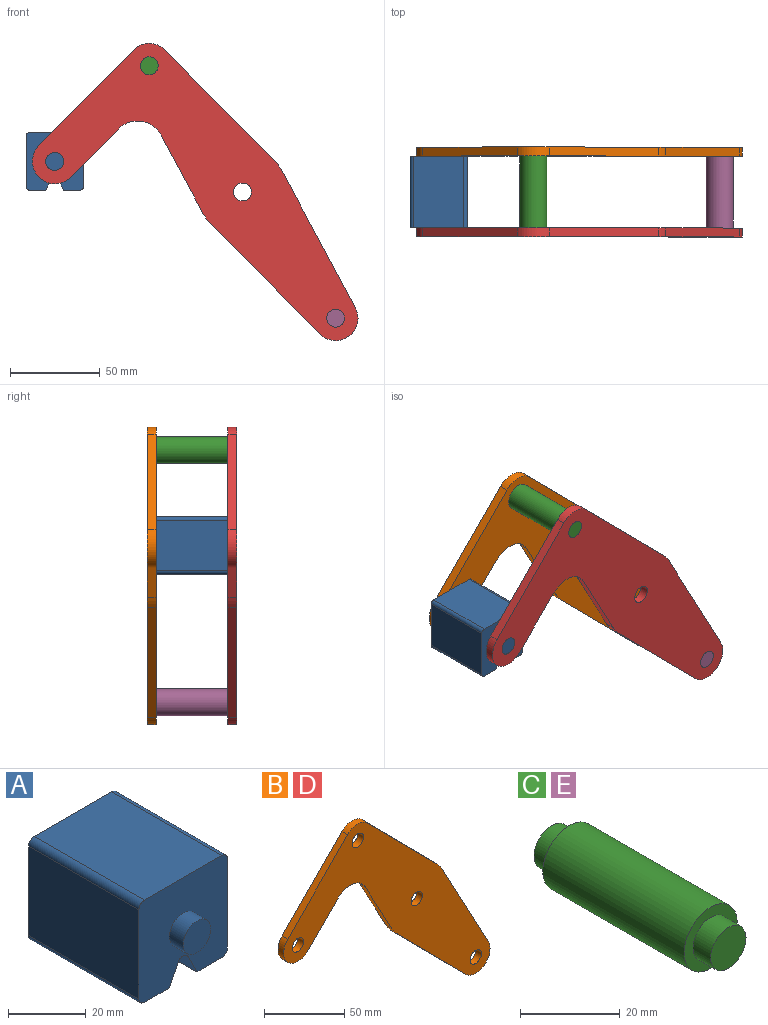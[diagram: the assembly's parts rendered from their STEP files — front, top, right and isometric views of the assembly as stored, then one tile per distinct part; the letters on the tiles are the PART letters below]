
ASSEMBLY  parts=5 mates=3
PART A: 18 faces, bbox 32.1x50x32.1 mm
  f0: plane 40x28.08mm, normal (1,0,0), area 1123.1mm2, adj f4,f10,f13,f14
  f1: plane 40x9.04mm, normal (0,0,-1), area 361.6mm2, adj f2,f4,f10,f14
  f2: plane 40x6.42mm, normal (-0.89,0,-0.45), area 287.2mm2, adj f1,f4,f10,f15
  f3: plane 40x6.42mm, normal (0.89,0,-0.45), area 287.2mm2, adj f4,f5,f10,f15
  f4: plane 32.08x32.08mm, normal (0,-1,0), area 900.6mm2, adj f0,f1,f2,f3,f5,f6,f7,f9
  f5: plane 40x9.04mm, normal (0,0,-1), area 361.6mm2, adj f3,f4,f10,f16
  f6: plane 40x28.08mm, normal (0,0,1), area 1123.1mm2, adj f4,f10,f13,f17
  f7: plane 40x28.08mm, normal (-1,0,0), area 1123.1mm2, adj f4,f10,f16,f17
  f8: plane 10x10mm, normal (0,-1,0), area 78.5mm2, adj f9
  f9: cylinder r=5mm len=10mm, axis (0,1,0), area 157.1mm2, adj f4,f8
  f10: plane 32.08x32.08mm, normal (0,1,0), area 900.6mm2, adj f0,f1,f2,f3,f5,f6,f7,f12
  f11: plane 10x10mm, normal (0,1,0), area 78.5mm2, adj f12
  f12: cylinder r=5mm len=10mm, axis (0,-1,0), area 157.1mm2, adj f10,f11
  f13: cylinder r=2mm len=40mm, axis (0,1,0), area 125.7mm2, adj f0,f4,f6,f10
  f14: cylinder r=2mm len=40mm, axis (0,-1,0), area 125.7mm2, adj f0,f1,f4,f10
  f15: cylinder r=2mm len=40mm, axis (0,1,0), area 177.1mm2, adj f2,f3,f4,f10
  f16: cylinder r=2mm len=40mm, axis (0,1,0), area 125.7mm2, adj f4,f5,f7,f10
  f17: cylinder r=2mm len=40mm, axis (0,-1,0), area 125.7mm2, adj f4,f6,f7,f10
PART B: 18 faces, bbox 181.7x5x165.8 mm
  f0: plane 43.49x23.35mm, normal (-0.88,0,-0.47), area 246.8mm2, adj f1,f14,f16,f17
  f1: cylinder r=25mm len=5.75mm, axis (0,1,0), area 35.8mm2, adj f0,f2,f16,f17
  f2: plane 61.6x60.87mm, normal (-0.71,0,-0.7), area 433mm2, adj f1,f3,f16,f17
  f3: cylinder r=12.5mm len=21.39mm, axis (0,1,0), area 178.4mm2, adj f2,f4,f16,f17
  f4: plane 76.3x40.96mm, normal (0.88,0,0.47), area 433mm2, adj f3,f5,f16,f17
  f5: cylinder r=25mm len=5.75mm, axis (0,1,0), area 35.8mm2, adj f4,f6,f16,f17
  f6: plane 61.6x60.87mm, normal (0.71,0,0.7), area 433mm2, adj f5,f7,f16,f17
  f7: cylinder r=12.5mm len=17.78mm, axis (0,1,0), area 98.9mm2, adj f6,f8,f16,f17
  f8: plane 53.35x52.71mm, normal (-0.71,0,0.7), area 375mm2, adj f7,f9,f16,f17
  f9: cylinder r=12.5mm len=21.39mm, axis (0,1,0), area 196.3mm2, adj f8,f10,f16,f17
  f10: plane 26.86x26.54mm, normal (0.71,0,-0.7), area 188.8mm2, adj f9,f14,f16,f17
  f11: cylinder r=5mm len=10mm, axis (0,1,0), area 157.1mm2, adj f16,f17
  f12: cylinder r=5mm len=10mm, axis (0,1,0), area 157.1mm2, adj f16,f17
  f13: cylinder r=5mm len=10mm, axis (0,1,0), area 157.1mm2, adj f16,f17
  f14: cylinder r=15mm len=23.89mm, axis (0,1,0), area 140.2mm2, adj f0,f10,f16,f17
  f15: cylinder r=5mm len=10mm, axis (0,1,0), area 157.1mm2, adj f16,f17
  f16: plane 181.66x165.78mm, normal (0,-1,0), area 8710.1mm2, adj f0,f1,f2,f3,f4,f5,f6,f7
  f17: plane 181.66x165.78mm, normal (0,1,0), area 8710.1mm2, adj f0,f1,f2,f3,f4,f5,f6,f7
PART C: 7 faces, bbox 15x50x15 mm
  f0: cylinder r=7.5mm len=40mm, axis (0,-1,0), area 1885mm2, adj f2,f5
  f1: cylinder r=5mm len=10mm, axis (0,1,0), area 157.1mm2, adj f2,f3
  f2: plane 15x15mm, normal (0,-1,0), area 98.2mm2, adj f0,f1
  f3: plane 10x10mm, normal (0,-1,0), area 78.5mm2, adj f1
  f4: cylinder r=5mm len=10mm, axis (0,-1,0), area 157.1mm2, adj f5,f6
  f5: plane 15x15mm, normal (0,1,0), area 98.2mm2, adj f0,f4
  f6: plane 10x10mm, normal (0,1,0), area 78.5mm2, adj f4
PART D: same geometry as B
PART E: same geometry as C
PLACE A t=(0,-20,0)mm
PLACE B t=(0,25,0)mm
PLACE C t=(0,-20,0)mm
PLACE D t=(0,-20,0)mm fixed
PLACE E t=(103.95,-20,-140.78)mm
MATE revolute B.f7 <-> C.f0  axis (0,-1,0) through (-51.98,20,70.39)mm
MATE fastened E.f0 <-> D.f3  axis (0,-1,0) through (51.98,-20,-70.39)mm
MATE revolute A.f9 <-> D.f9  axis (0,-1,0) through (-104.69,-20,17.04)mm
